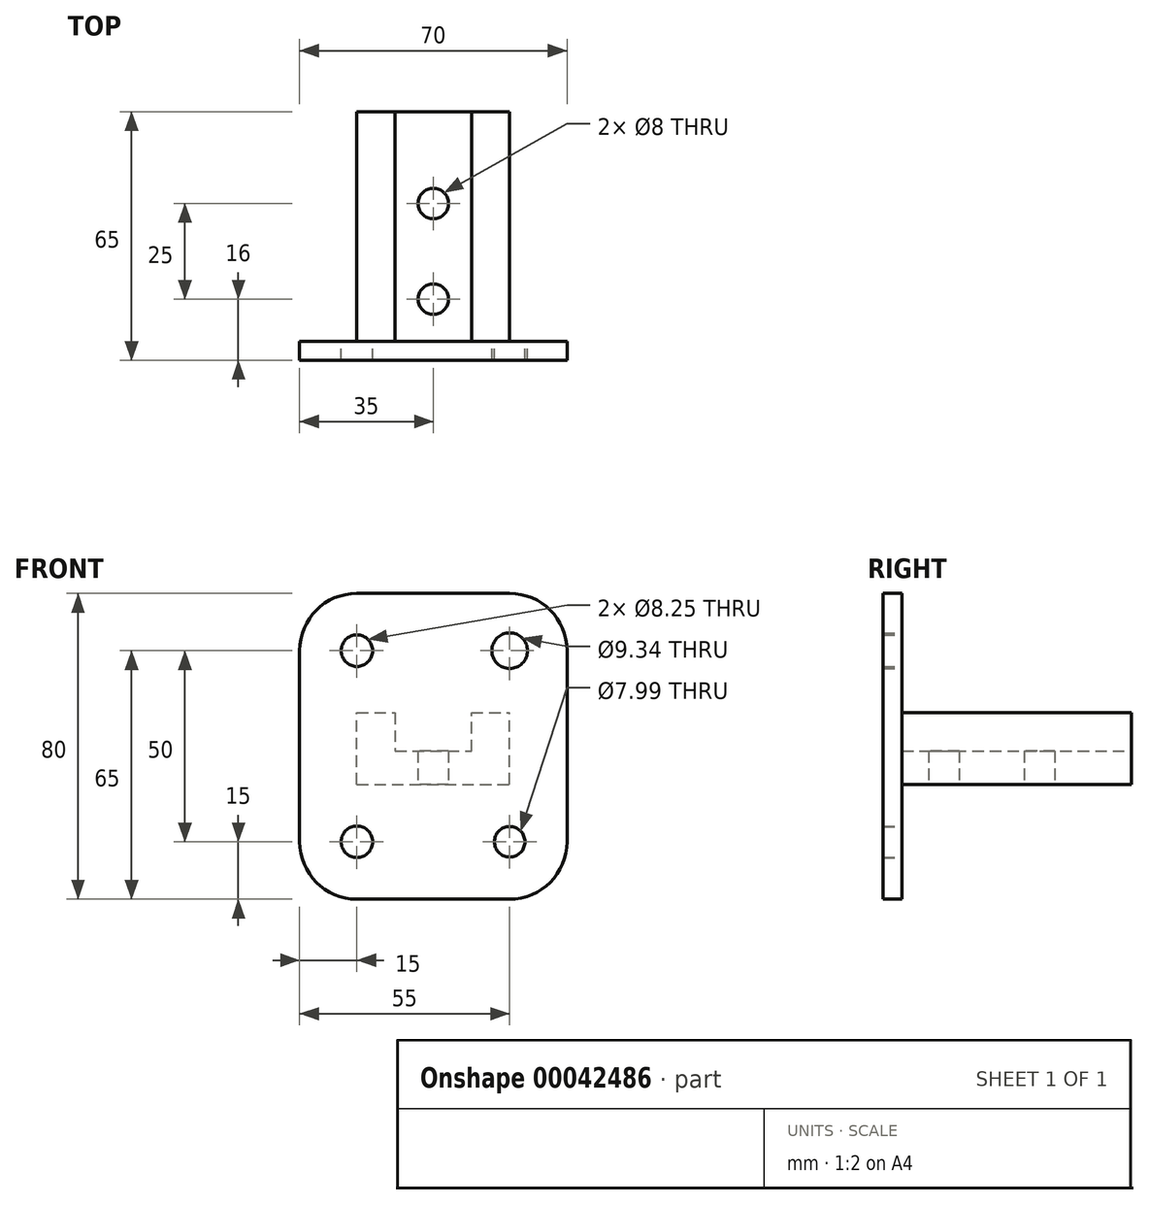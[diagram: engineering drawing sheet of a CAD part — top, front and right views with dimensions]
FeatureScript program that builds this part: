
annotation { "Feature Type Name" : "Feature", "Feature Type Description" : "" }
export const myFeature = defineFeature(function(context is Context, id is Id, definition is map)
    precondition{}
    {
        {
            var Q0;
            Q0=qCreatedBy(makeId("Front.planeOp"),FACE);
            var sketch = newSketch(context, id + "F0", { "sketchPlane" : qUnion([Q0])});
            skLineSegment(sketch, "E0.bottom", {"start": v(-20, 0) * mm, "end": v(20, 0) * mm});
            skLineSegment(sketch, "E0.top", {"start": v(-20, 18.73) * mm, "end": v(-10, 18.73) * mm});
            skLineSegment(sketch, "E0.left", {"start": v(-20, 0) * mm, "end": v(-20, 18.73) * mm});
            skLineSegment(sketch, "E0.right", {"start": v(20, 0) * mm, "end": v(20, 18.73) * mm});
            skLineSegment(sketch, "E1", {"start": v(-10, 18.73) * mm, "end": v(-10, 8.73) * mm});
            skLineSegment(sketch, "E2", {"start": v(-10, 8.73) * mm, "end": v(10, 8.73) * mm});
            skLineSegment(sketch, "E3", {"start": v(10, 8.73) * mm, "end": v(10, 18.73) * mm});
            skLineSegment(sketch, "E4.trimOffspring", {"start": v(10, 18.73) * mm, "end": v(20, 18.73) * mm});
            skSolve(sketch);
        }
        {
            var Q0;
            Q0 = qSketchRegion(id + "F0", true);
            extrude(context, id + "F1", {"entities" : qUnion([Q0]), "depth" : 60 * mm});
        }
        {
            var Q0;
            Q0=makeQuery(id+"F1.opExtrude","CAP_FACE",FACE,{"disambiguationData":[OSD([sQuery(id+"F0.wireOp",EDGE,"E0.bottom"),sQuery(id+"F0.wireOp",EDGE,"E0.top"),sQuery(id+"F0.wireOp",EDGE,"E0.left"),sQuery(id+"F0.wireOp",EDGE,"E0.right"),sQuery(id+"F0.wireOp",EDGE,"E1"),sQuery(id+"F0.wireOp",EDGE,"E2"),sQuery(id+"F0.wireOp",EDGE,"E3"),sQuery(id+"F0.wireOp",EDGE,"E4.trimOffspring")])],"isStart":false});
            var sketch = newSketch(context, id + "F2", { "sketchPlane" : qUnion([Q0])});
            skLineSegment(sketch, "E5.bottom", {"start": v(-20, 50) * mm, "end": v(20, 50) * mm});
            skLineSegment(sketch, "E5.top", {"start": v(-20, -30) * mm, "end": v(20, -30) * mm});
            skLineSegment(sketch, "E5.left", {"start": v(-35, 35) * mm, "end": v(-35, -15) * mm});
            skLineSegment(sketch, "E5.right", {"start": v(35, 35) * mm, "end": v(35, -15) * mm});
            skPoint(sketch, "E6.visualSharp", {"position": v(-35, 50) * mm});
            skArc(sketch, "E6.filletArc", {"start": v(-20, 50) * mm, "mid": v(-30.6, 45.6) * mm, "end": v(-35, 35) * mm});
            skPoint(sketch, "E7.visualSharp", {"position": v(35, 50) * mm});
            skArc(sketch, "E7.filletArc", {"start": v(35, 35) * mm, "mid": v(30.6, 45.6) * mm, "end": v(20, 50) * mm});
            skPoint(sketch, "E8.visualSharp", {"position": v(-35, -30) * mm});
            skArc(sketch, "E8.filletArc", {"start": v(-35, -15) * mm, "mid": v(-30.6, -25.6) * mm, "end": v(-20, -30) * mm});
            skPoint(sketch, "E9.visualSharp", {"position": v(35, -30) * mm});
            skArc(sketch, "E9.filletArc", {"start": v(20, -30) * mm, "mid": v(30.6, -25.6) * mm, "end": v(35, -15) * mm});
            skCircle(sketch, "E10", {"center": v(-20, 35) * mm, "radius": 4.12 * mm});
            skCircle(sketch, "E11", {"center": v(20, 35) * mm, "radius": 4.67 * mm});
            skCircle(sketch, "E12", {"center": v(20, -15) * mm, "radius": 4 * mm});
            skCircle(sketch, "E13", {"center": v(-20, -15) * mm, "radius": 4.12 * mm});
            skSolve(sketch);
        }
        {
            var Q0;
            Q0 = qSketchRegion(id + "F2", true);
            extrude(context, id + "F3", {"entities" : qUnion([Q0]), "operationType" : NewBodyOperationType.ADD, "depth" : 5 * mm});
        }
        {
            var Q0;
            Q0=qCreatedBy(makeId("Top.planeOp"),FACE);
            var sketch = newSketch(context, id + "F4", { "sketchPlane" : qUnion([Q0])});
            skCircle(sketch, "E14", {"center": v(0, -49) * mm, "radius": 4 * mm});
            skCircle(sketch, "E15", {"center": v(0, -24) * mm, "radius": 4 * mm});
            skSolve(sketch);
        }
        {
            var Q0;
            Q0 = qSketchRegion(id + "F4", true);
            extrude(context, id + "F5", {"entities" : qUnion([Q0]), "operationType" : NewBodyOperationType.REMOVE, "endBound" : BoundingType.THROUGH_ALL, "depth" : 25 * mm});
        }
    });
